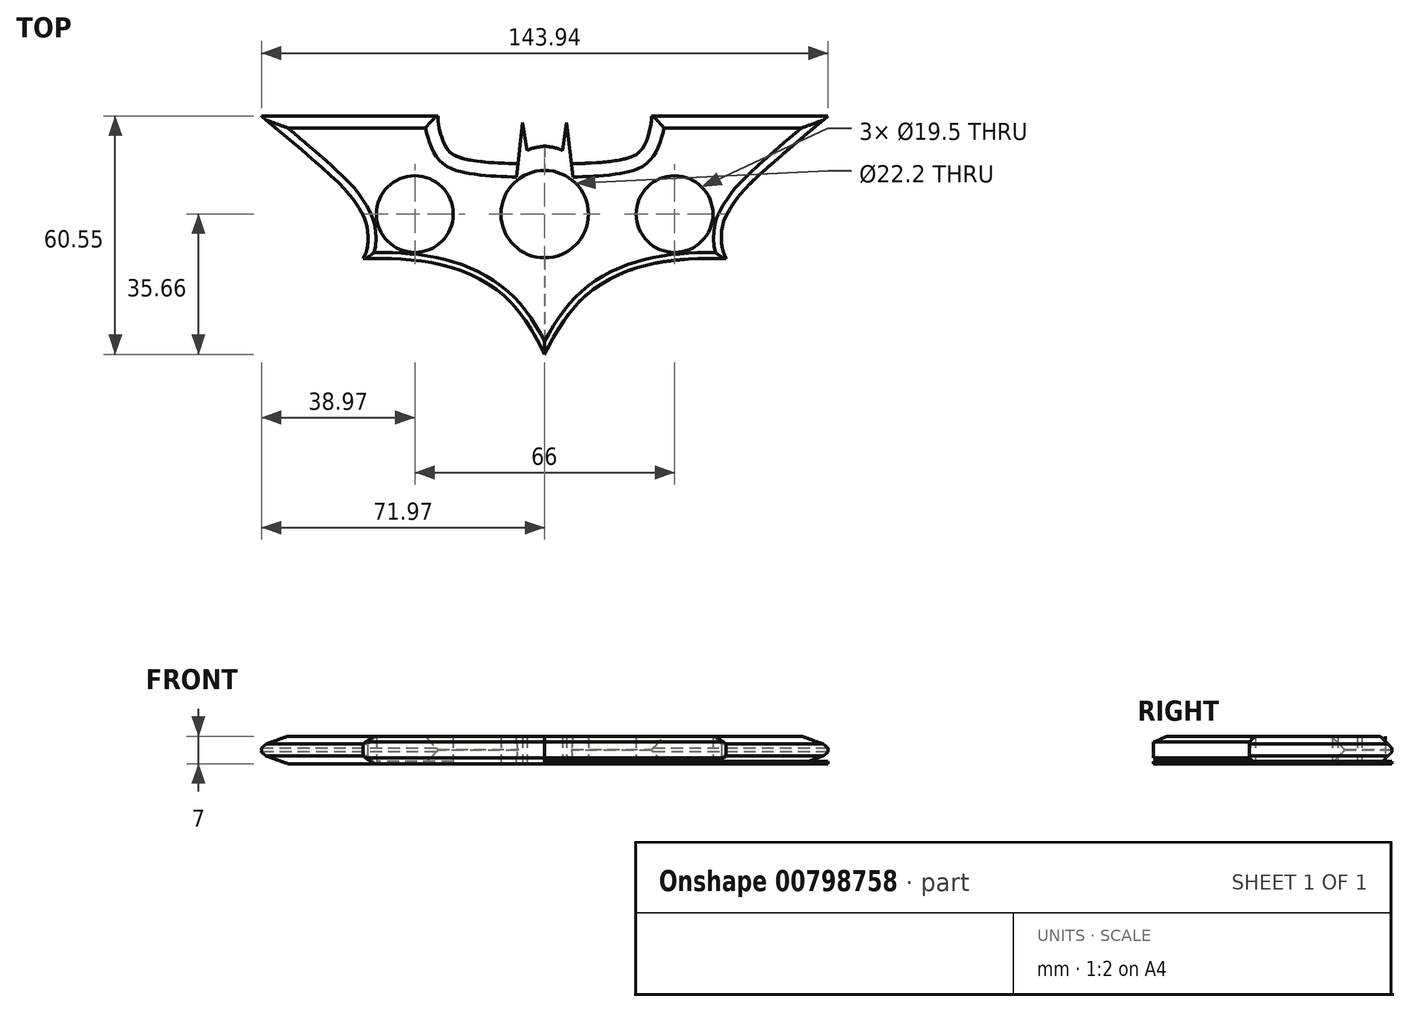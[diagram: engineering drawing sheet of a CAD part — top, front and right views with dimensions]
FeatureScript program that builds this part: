
annotation { "Feature Type Name" : "Feature", "Feature Type Description" : "" }
export const myFeature = defineFeature(function(context is Context, id is Id, definition is map)
    precondition{}
    {
        {
            var Q0;
            Q0=qCreatedBy(makeId("Top.planeOp"),FACE);
            var sketch = newSketch(context, id + "F0", { "sketchPlane" : qUnion([Q0])});
            skCircle(sketch, "E0", {"center": v(0, 0) * mm, "radius": 11.1 * mm});
            skLineSegment(sketch, "E1", {"start": v(0, 0) * mm, "end": v(-33, 0) * mm});
            skCircle(sketch, "E2", {"center": v(-33, 0) * mm, "radius": 9.75 * mm});
            skFitSpline(sketch, "E3", {"points": [v(0, 17.3) * mm, v(-1.4, 17.06) * mm, v(-3.35, 16.66) * mm, v(-4.47, 16.18) * mm], "startDerivative": vector(-4.1, -0.71) * mm, "endDerivative": vector(-3.42, -1.73) * mm});
            skLineSegment(sketch, "E4", {"start": v(-4.47, 16.18) * mm, "end": v(-5.6, 23.2) * mm});
            skLineSegment(sketch, "E5", {"start": v(-5.6, 23.2) * mm, "end": v(-6.81, 12.87) * mm});
            skFitSpline(sketch, "E6", {"points": [v(-6.81, 12.87) * mm, v(-9.23, 12.87) * mm, v(-21.65, 14.4) * mm, v(-25.44, 17.7) * mm, v(-26.98, 22.8) * mm, v(-27.14, 24.89) * mm], "startDerivative": vector(-12.54, -0.34) * mm, "endDerivative": vector(-0.24, 13.93) * mm});
            skLineSegment(sketch, "E7", {"start": v(-27.14, 24.89) * mm, "end": v(-71.97, 24.89) * mm});
            skFitSpline(sketch, "E8", {"points": [v(-46.1, -11.34) * mm, v(-45.14, -8.77) * mm, v(-44.92, -4.9) * mm, v(-45.67, -1.37) * mm, v(-47.6, 2.16) * mm, v(-51.35, 6.88) * mm, v(-71.97, 24.89) * mm], "startDerivative": vector(10.26, 21.98) * mm, "endDerivative": vector(-72.38, 60.38) * mm});
            skFitSpline(sketch, "E9", {"points": [v(-46.1, -11.34) * mm, v(-38.06, -11.34) * mm, v(-26.96, -12.72) * mm, v(-16.86, -16.33) * mm, v(-8.01, -23.07) * mm, v(-1.9, -31.92) * mm, v(0, -35.66) * mm], "startDerivative": vector(49.03, 1.23) * mm, "endDerivative": vector(13.98, -29.3) * mm});
            skLineSegment(sketch, "E10", {"start": v(0, 17.3) * mm, "end": v(0, -35.66) * mm});
            skLineSegment(sketch, "E11.MirrorCS", {"start": v(27.14, 24.89) * mm, "end": v(71.97, 24.89) * mm});
            skFitSpline(sketch, "E12.MirrorCS", {"points": [v(46.1, -11.34) * mm, v(45.14, -8.77) * mm, v(44.92, -4.9) * mm, v(45.67, -1.37) * mm, v(47.6, 2.16) * mm, v(51.35, 6.88) * mm, v(71.97, 24.89) * mm], "startDerivative": vector(-10.26, 21.98) * mm, "endDerivative": vector(72.38, 60.38) * mm});
            skFitSpline(sketch, "E13.MirrorCS", {"points": [v(6.81, 12.87) * mm, v(9.23, 12.87) * mm, v(21.65, 14.4) * mm, v(25.44, 17.7) * mm, v(26.98, 22.8) * mm, v(27.14, 24.89) * mm], "startDerivative": vector(12.54, -0.34) * mm, "endDerivative": vector(0.24, 13.93) * mm});
            skLineSegment(sketch, "E14.MirrorCS", {"start": v(5.6, 23.2) * mm, "end": v(6.81, 12.87) * mm});
            skLineSegment(sketch, "E15.MirrorCS", {"start": v(4.47, 16.18) * mm, "end": v(5.6, 23.2) * mm});
            skFitSpline(sketch, "E16.MirrorCS", {"points": [v(0, 17.3) * mm, v(1.4, 17.06) * mm, v(3.35, 16.66) * mm, v(4.47, 16.18) * mm], "startDerivative": vector(4.1, -0.71) * mm, "endDerivative": vector(3.42, -1.73) * mm});
            skFitSpline(sketch, "E17.MirrorCS", {"points": [v(46.1, -11.34) * mm, v(38.06, -11.34) * mm, v(26.96, -12.72) * mm, v(16.86, -16.33) * mm, v(8.01, -23.07) * mm, v(1.9, -31.92) * mm, v(0, -35.66) * mm], "startDerivative": vector(-49.03, 1.23) * mm, "endDerivative": vector(-13.98, -29.3) * mm});
            skCircle(sketch, "E18.MirrorC", {"center": v(33, 0) * mm, "radius": 9.75 * mm});
            skSolve(sketch);
        }
        {
            var Q0;
            Q0=makeQuery(id+"F0.imprint","IMPRINT",FACE,{"disambiguationData":[TD([[makeQuery(id+"F0.imprint","IMPRINT",EDGE,{"derivedFrom":sQuery(id+"F0.wireOp",EDGE,"E2")}),-1.0]])]});
            var Q1;
            Q1=makeQuery(id+"F0.imprint","IMPRINT",FACE,{"disambiguationData":[TD([[makeQuery(id+"F0.imprint","IMPRINT",EDGE,{"derivedFrom":sQuery(id+"F0.wireOp",EDGE,"E11.MirrorCS")}),-1.0]])]});
            extrude(context, id + "F1", {"entities" : qUnion([Q0, Q1]), "depth" : 7 * mm, "offsetDistance" : 25 * mm});
        }
        {
            var Q0;
            Q0=makeQuery(id+"F0.imprint","IMPRINT",FACE,{"disambiguationData":[TD([[makeQuery(id+"F0.imprint","IMPRINT",EDGE,{"derivedFrom":sQuery(id+"F0.wireOp",EDGE,"E18.MirrorC")}),-1.0]])]});
            var Q1;
            Q1=makeQuery(id+"F0.imprint","IMPRINT",FACE,{"disambiguationData":[TD([[makeQuery(id+"F0.imprint","IMPRINT",EDGE,{"derivedFrom":sQuery(id+"F0.wireOp",EDGE,"E2")}),1.0]])]});
            var Q2;
            Q2=sQuery(id+"F0.wireOp",EDGE,"E2");
            var Q3;
            Q3=sQuery(id+"F0.wireOp",EDGE,"E18.MirrorC");
            extrude(context, id + "F2", {"entities" : qUnion([Q0, Q1]), "surfaceOperationType" : NewSurfaceOperationType.ADD, "surfaceEntities" : qUnion([Q2, Q3]), "depth" : 0.6 * mm, "offsetDistance" : 25 * mm});
        }
        {
            var Q0;
            Q0=makeQuery(id+"F1.opExtrude","CAP_EDGE",EDGE,{"disambiguationData":[OSD([sQuery(id+"F0.wireOp",EDGE,"E7")])],"isStart":false});
            var Q1;
            Q1=makeQuery(id+"F1.opExtrude","CAP_EDGE",EDGE,{"disambiguationData":[OSD([sQuery(id+"F0.wireOp",EDGE,"E7")])],"isStart":true});
            var Q2;
            Q2=makeQuery(id+"F1.opExtrude","CAP_EDGE",EDGE,{"disambiguationData":[OSD([sQuery(id+"F0.wireOp",EDGE,"E11.MirrorCS")])],"isStart":false});
            var Q3;
            Q3=makeQuery(id+"F1.opExtrude","CAP_EDGE",EDGE,{"disambiguationData":[OSD([sQuery(id+"F0.wireOp",EDGE,"E11.MirrorCS")])],"isStart":true});
            chamfer(context, id + "F3", {"entities" : qUnion([Q0, Q1, Q2, Q3]), "width" : 3 * mm, "tangentPropagation" : true});
        }
        {
            var Q0;
            Q0=makeQuery(id+"F1.opExtrude","CAP_EDGE",EDGE,{"disambiguationData":[OSD([sQuery(id+"F0.wireOp",EDGE,"E13.MirrorCS")])],"isStart":false});
            var Q1;
            Q1=makeQuery(id+"F1.opExtrude","CAP_EDGE",EDGE,{"disambiguationData":[OSD([sQuery(id+"F0.wireOp",EDGE,"E13.MirrorCS")])],"isStart":true});
            var Q2;
            Q2=makeQuery(id+"F1.opExtrude","CAP_EDGE",EDGE,{"disambiguationData":[OSD([sQuery(id+"F0.wireOp",EDGE,"E6")])],"isStart":false});
            var Q3;
            Q3=makeQuery(id+"F1.opExtrude","CAP_EDGE",EDGE,{"disambiguationData":[OSD([sQuery(id+"F0.wireOp",EDGE,"E6")])],"isStart":true});
            chamfer(context, id + "F4", {"entities" : qUnion([Q0, Q1, Q2, Q3]), "width" : 3.4 * mm, "tangentPropagation" : true});
        }
        {
            var Q0;
            Q0=makeQuery(id+"F1.opExtrude","CAP_EDGE",EDGE,{"disambiguationData":[OSD([sQuery(id+"F0.wireOp",EDGE,"E12.MirrorCS")])],"isStart":false});
            var Q1;
            Q1=makeQuery(id+"F1.opExtrude","CAP_EDGE",EDGE,{"disambiguationData":[OSD([sQuery(id+"F0.wireOp",EDGE,"E12.MirrorCS")])],"isStart":true});
            var Q2;
            Q2=makeQuery(id+"F1.opExtrude","CAP_EDGE",EDGE,{"disambiguationData":[OSD([sQuery(id+"F0.wireOp",EDGE,"E8")])],"isStart":false});
            var Q3;
            Q3=makeQuery(id+"F1.opExtrude","CAP_EDGE",EDGE,{"disambiguationData":[OSD([sQuery(id+"F0.wireOp",EDGE,"E8")])],"isStart":true});
            chamfer(context, id + "F5", {"entities" : qUnion([Q0, Q1, Q2, Q3]), "width" : 2 * mm, "tangentPropagation" : true});
        }
        {
            var Q0;
            Q0=makeQuery(id+"F1.opExtrude","CAP_EDGE",EDGE,{"disambiguationData":[OSD([sQuery(id+"F0.wireOp",EDGE,"E9")])],"isStart":false});
            var Q1;
            Q1=makeQuery(id+"F1.opExtrude","CAP_EDGE",EDGE,{"disambiguationData":[OSD([sQuery(id+"F0.wireOp",EDGE,"E17.MirrorCS")])],"isStart":false});
            var Q2;
            Q2=makeQuery(id+"F1.opExtrude","CAP_EDGE",EDGE,{"disambiguationData":[OSD([sQuery(id+"F0.wireOp",EDGE,"E17.MirrorCS")])],"isStart":true});
            var Q3;
            Q3=makeQuery(id+"F1.opExtrude","CAP_EDGE",EDGE,{"disambiguationData":[OSD([sQuery(id+"F0.wireOp",EDGE,"E9")])],"isStart":true});
            chamfer(context, id + "F6", {"entities" : qUnion([Q0, Q1, Q2, Q3]), "width" : 1.5 * mm, "tangentPropagation" : true});
        }
    });
